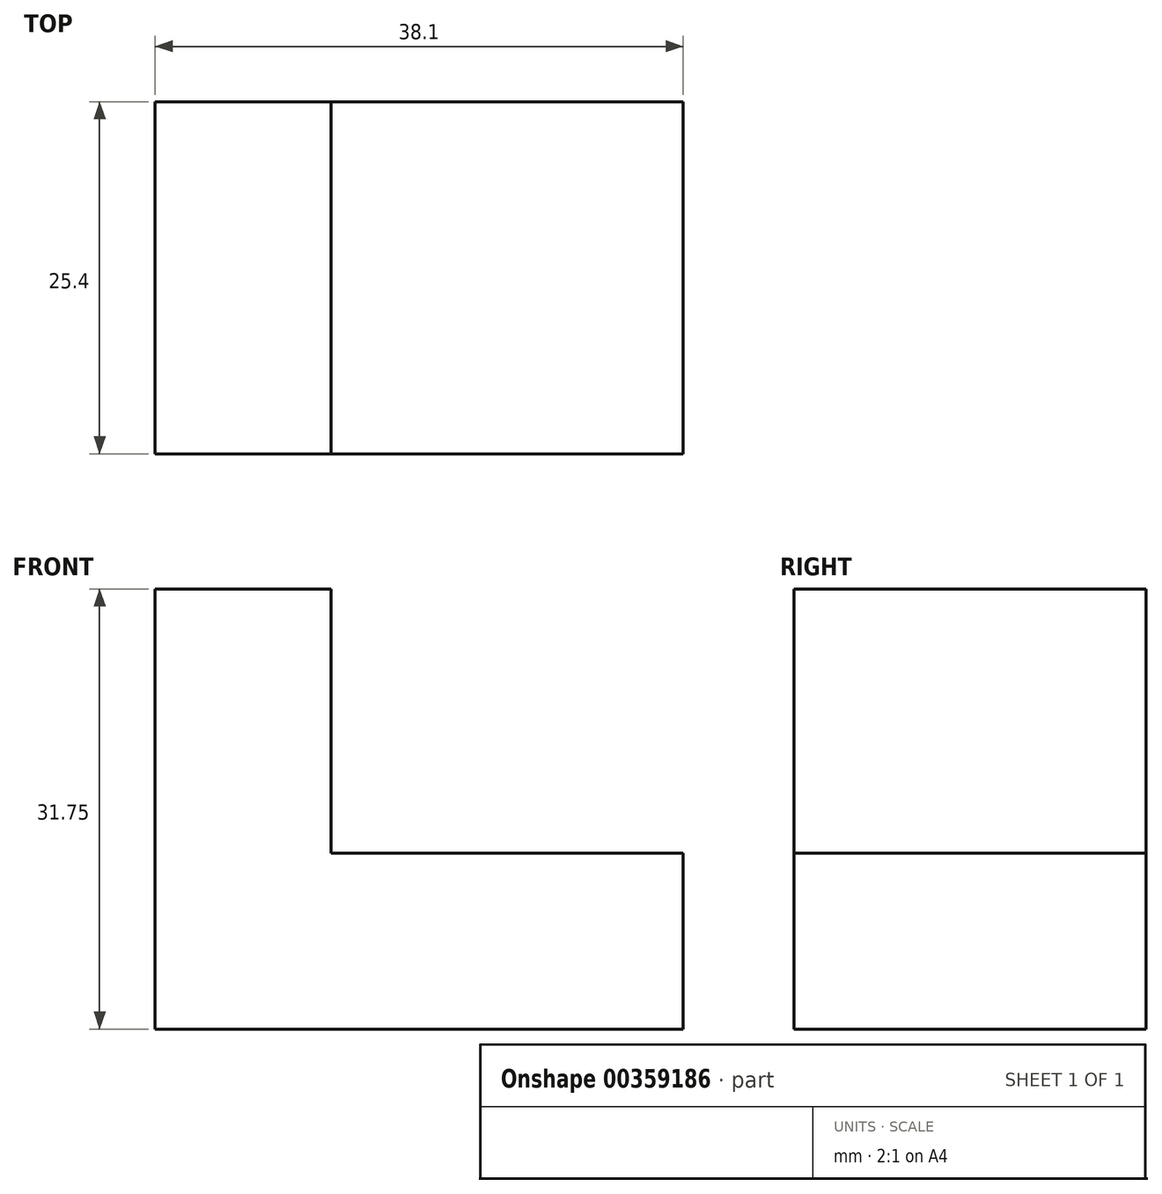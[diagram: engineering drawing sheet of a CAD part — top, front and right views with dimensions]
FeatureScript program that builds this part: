
annotation { "Feature Type Name" : "Feature", "Feature Type Description" : "" }
export const myFeature = defineFeature(function(context is Context, id is Id, definition is map)
    precondition{}
    {
        {
            var Q0;
            Q0=qCreatedBy(makeId("Front.planeOp"),FACE);
            var sketch = newSketch(context, id + "F0", { "sketchPlane" : qUnion([Q0])});
            skLineSegment(sketch, "E0.bottom", {"start": v(0, 31.75) * mm, "end": v(38.1, 31.75) * mm});
            skLineSegment(sketch, "E0.top", {"start": v(0, 0) * mm, "end": v(38.1, 0) * mm});
            skLineSegment(sketch, "E0.left", {"start": v(0, 31.75) * mm, "end": v(0, 0) * mm});
            skLineSegment(sketch, "E0.right", {"start": v(38.1, 31.75) * mm, "end": v(38.1, 0) * mm});
            skLineSegment(sketch, "E1", {"start": v(12.7, 31.75) * mm, "end": v(12.7, 12.7) * mm});
            skLineSegment(sketch, "E2", {"start": v(12.7, 12.7) * mm, "end": v(38.1, 12.7) * mm});
            skSolve(sketch);
        }
        {
            var Q0;
            {var subQ1=sQuery(id+"F0.wireOp",EDGE,"E0.top");Q0=makeQuery(id+"F0.imprint","IMPRINT",FACE,{"disambiguationData":[TD([[makeQuery(id+"F0.imprint","IMPRINT",EDGE,{"derivedFrom":subQ1}),1.0]])]});}
            var sketch = newSketch(context, id + "F1", { "sketchPlane" : qUnion([Q0])});
            skSolve(sketch);
        }
        {
            var Q0;
            Q0 = qSketchRegion(id + "F1", true);
            var Q1;
            {var subQ1=sQuery(id+"F0.wireOp",EDGE,"E0.top");Q1=makeQuery(id+"F0.imprint","IMPRINT",FACE,{"disambiguationData":[TD([[makeQuery(id+"F0.imprint","IMPRINT",EDGE,{"derivedFrom":subQ1}),1.0]])]});}
            extrude(context, id + "F2", {"entities" : qUnion([Q0, Q1]), "depth" : 25.4 * mm});
        }
    });
